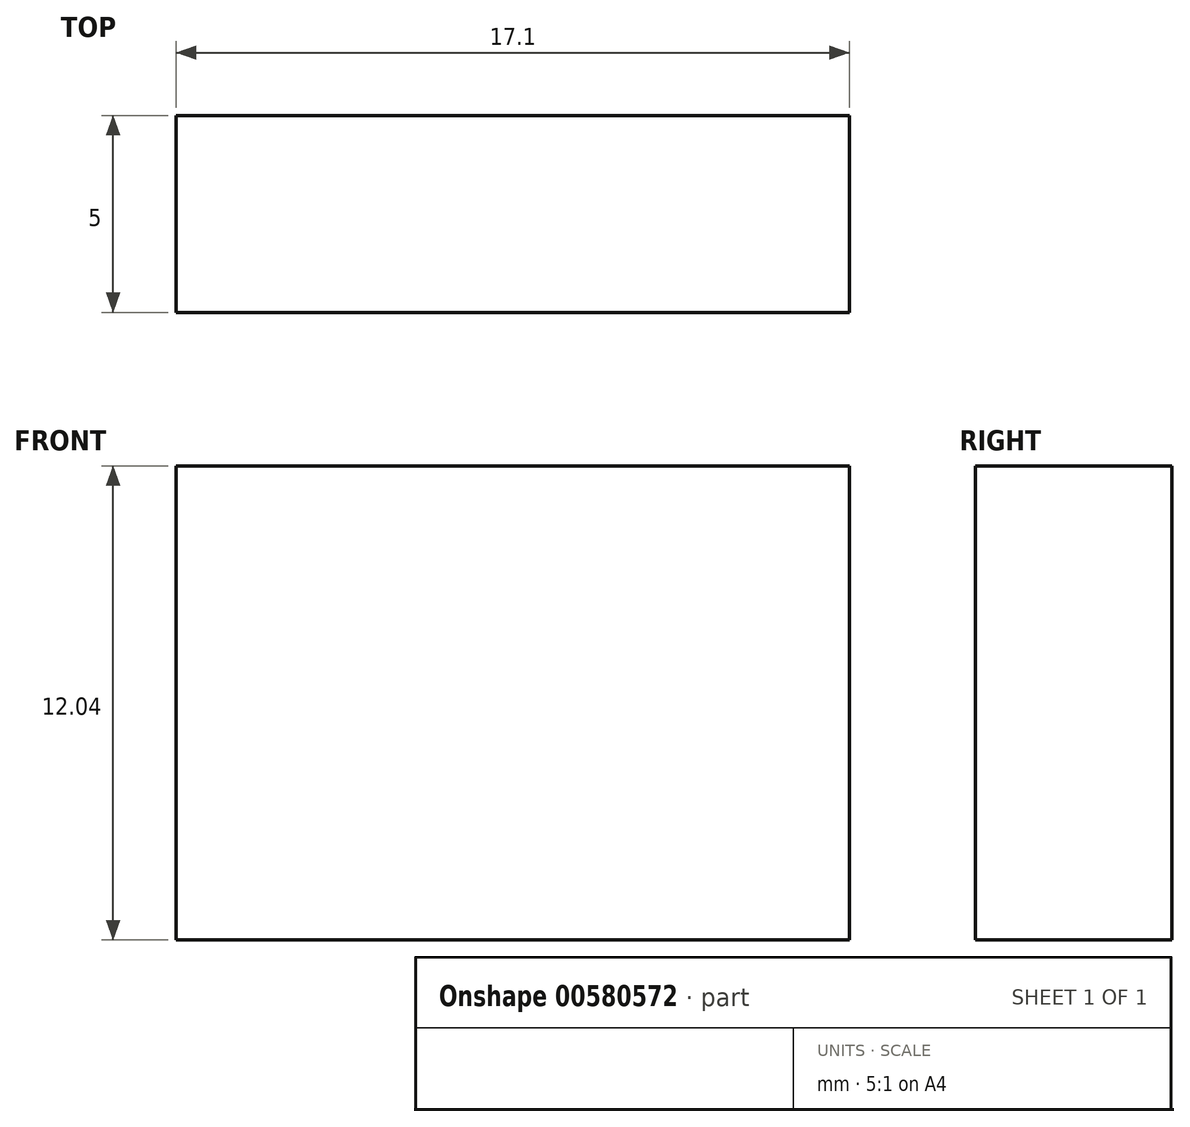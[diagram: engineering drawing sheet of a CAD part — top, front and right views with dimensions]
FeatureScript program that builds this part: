
annotation { "Feature Type Name" : "Feature", "Feature Type Description" : "" }
export const myFeature = defineFeature(function(context is Context, id is Id, definition is map)
    precondition{}
    {
        {
            var Q0;
            Q0=qCreatedBy(makeId("Front.planeOp"),FACE);
            var sketch = newSketch(context, id + "F0", { "sketchPlane" : qUnion([Q0])});
            skLineSegment(sketch, "E0.bottom", {"start": v(8.55, -6.02) * mm, "end": v(-8.55, -6.02) * mm});
            skLineSegment(sketch, "E0.top", {"start": v(8.55, 6.02) * mm, "end": v(-8.55, 6.02) * mm});
            skLineSegment(sketch, "E0.left", {"start": v(8.55, -6.02) * mm, "end": v(8.55, 6.02) * mm});
            skLineSegment(sketch, "E0.right", {"start": v(-8.55, -6.02) * mm, "end": v(-8.55, 6.02) * mm});
            skPoint(sketch, "E0.middle", {"position": v(0, 0) * mm});
            skSolve(sketch);
        }
        {
            var Q0;
            Q0 = qSketchRegion(id + "F0", true);
            extrude(context, id + "F1", {"entities" : qUnion([Q0]), "depth" : 5 * mm, "offsetDistance" : 25 * mm});
        }
    });
